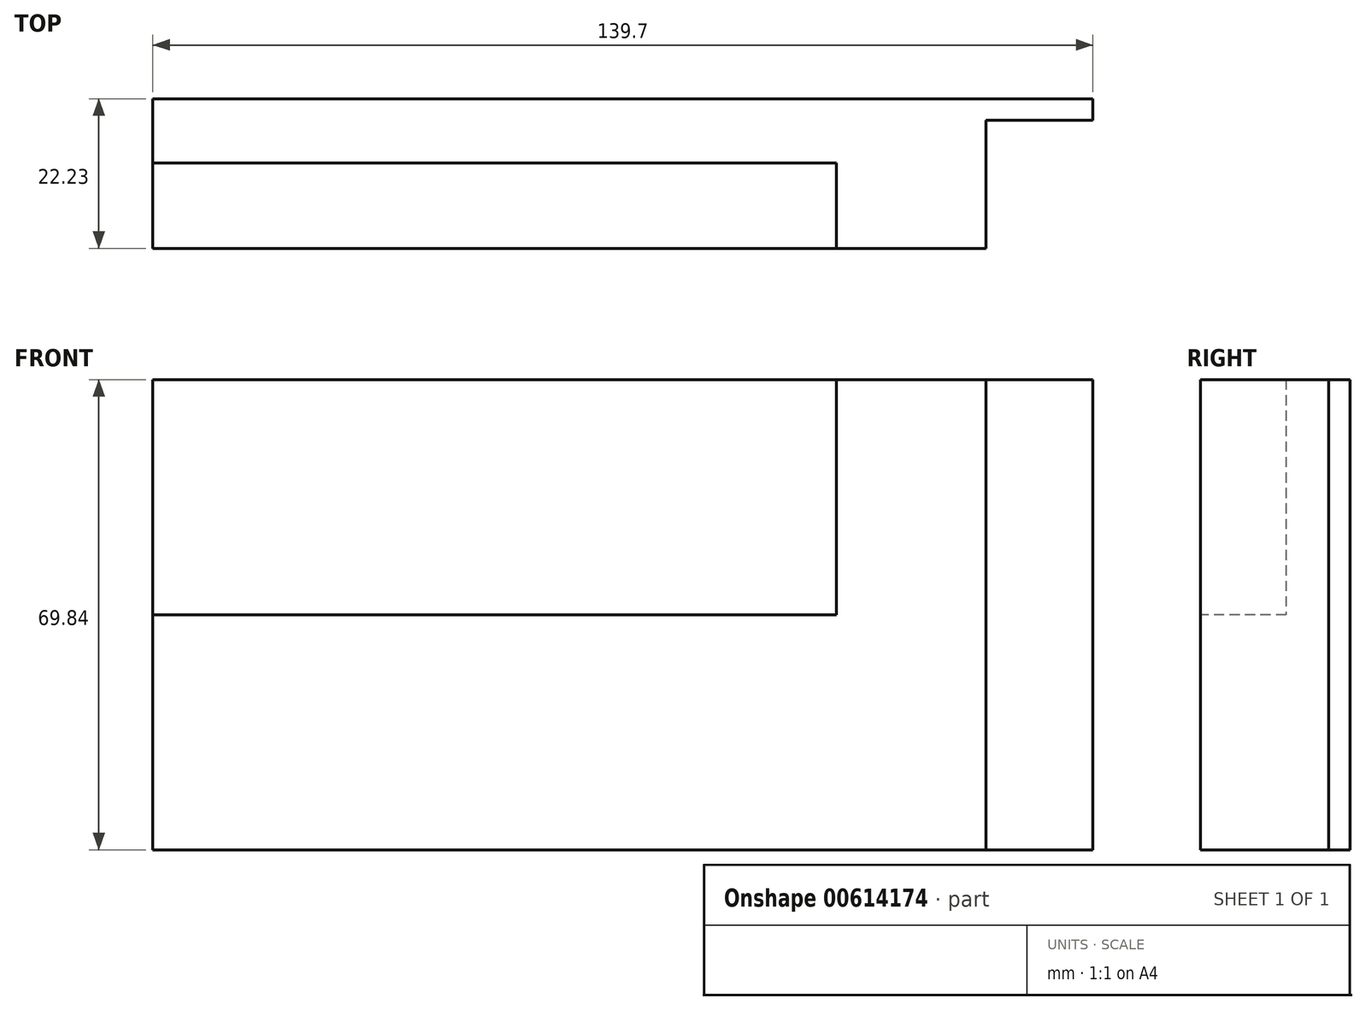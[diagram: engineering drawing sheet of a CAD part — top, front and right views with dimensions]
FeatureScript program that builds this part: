
annotation { "Feature Type Name" : "Feature", "Feature Type Description" : "" }
export const myFeature = defineFeature(function(context is Context, id is Id, definition is map)
    precondition{}
    {
        {
            var Q0;
            Q0=qCreatedBy(makeId("Front.planeOp"),FACE);
            var sketch = newSketch(context, id + "F0", { "sketchPlane" : qUnion([Q0])});
            skLineSegment(sketch, "E0.bottom", {"start": v(69.85, 34.93) * mm, "end": v(-69.85, 34.93) * mm});
            skLineSegment(sketch, "E0.top", {"start": v(69.85, -34.93) * mm, "end": v(-69.85, -34.93) * mm});
            skLineSegment(sketch, "E0.left", {"start": v(69.85, 34.93) * mm, "end": v(69.85, -34.92) * mm});
            skLineSegment(sketch, "E0.right", {"start": v(-69.85, 34.93) * mm, "end": v(-69.85, -34.93) * mm});
            skPoint(sketch, "E0.middle", {"position": v(0, 0) * mm});
            skSolve(sketch);
        }
        {
            var Q0;
            Q0 = qSketchRegion(id + "F0", true);
            extrude(context, id + "F1", {"entities" : qUnion([Q0]), "depth" : 22.22 * mm, "offsetDistance" : 25.4 * mm});
        }
        {
            var Q0;
            Q0=makeQuery(id+"F1.opExtrude","CAP_FACE",FACE,{"disambiguationData":[OSD([sQuery(id+"F0.wireOp",EDGE,"E0.bottom"),sQuery(id+"F0.wireOp",EDGE,"E0.top"),sQuery(id+"F0.wireOp",EDGE,"E0.left"),sQuery(id+"F0.wireOp",EDGE,"E0.right")])],"isStart":false});
            var sketch = newSketch(context, id + "F2", { "sketchPlane" : qUnion([Q0])});
            skLineSegment(sketch, "E1.bottom", {"start": v(-69.85, 34.93) * mm, "end": v(31.75, 34.93) * mm});
            skLineSegment(sketch, "E1.top", {"start": v(-69.85, 0) * mm, "end": v(31.75, 0) * mm});
            skLineSegment(sketch, "E1.left", {"start": v(-69.85, 34.93) * mm, "end": v(-69.85, 0) * mm});
            skLineSegment(sketch, "E1.right", {"start": v(31.75, 34.93) * mm, "end": v(31.75, 0) * mm});
            skSolve(sketch);
        }
        {
            var Q0;
            Q0 = qSketchRegion(id + "F2", true);
            extrude(context, id + "F3", {"entities" : qUnion([Q0]), "operationType" : NewBodyOperationType.REMOVE, "oppositeDirection" : true, "depth" : 12.7 * mm, "offsetDistance" : 25.4 * mm});
        }
        {
            var Q0;
            Q0=makeQuery(id+"F1.opExtrude","SWEPT_FACE",FACE,{"disambiguationData":[OSD([sQuery(id+"F0.wireOp",EDGE,"E0.bottom")])]});
            var sketch = newSketch(context, id + "F4", { "sketchPlane" : qUnion([Q0])});
            skLineSegment(sketch, "E2.bottom", {"start": v(69.85, -22.23) * mm, "end": v(53.98, -22.23) * mm});
            skLineSegment(sketch, "E2.top", {"start": v(69.85, -3.18) * mm, "end": v(53.98, -3.18) * mm});
            skLineSegment(sketch, "E2.left", {"start": v(69.85, -22.23) * mm, "end": v(69.85, -3.18) * mm});
            skLineSegment(sketch, "E2.right", {"start": v(53.98, -22.23) * mm, "end": v(53.98, -3.18) * mm});
            skSolve(sketch);
        }
        {
            var Q0;
            Q0 = qSketchRegion(id + "F4", true);
            extrude(context, id + "F5", {"entities" : qUnion([Q0]), "operationType" : NewBodyOperationType.REMOVE, "oppositeDirection" : true, "depth" : 127 * mm, "offsetDistance" : 25.4 * mm});
        }
    });
